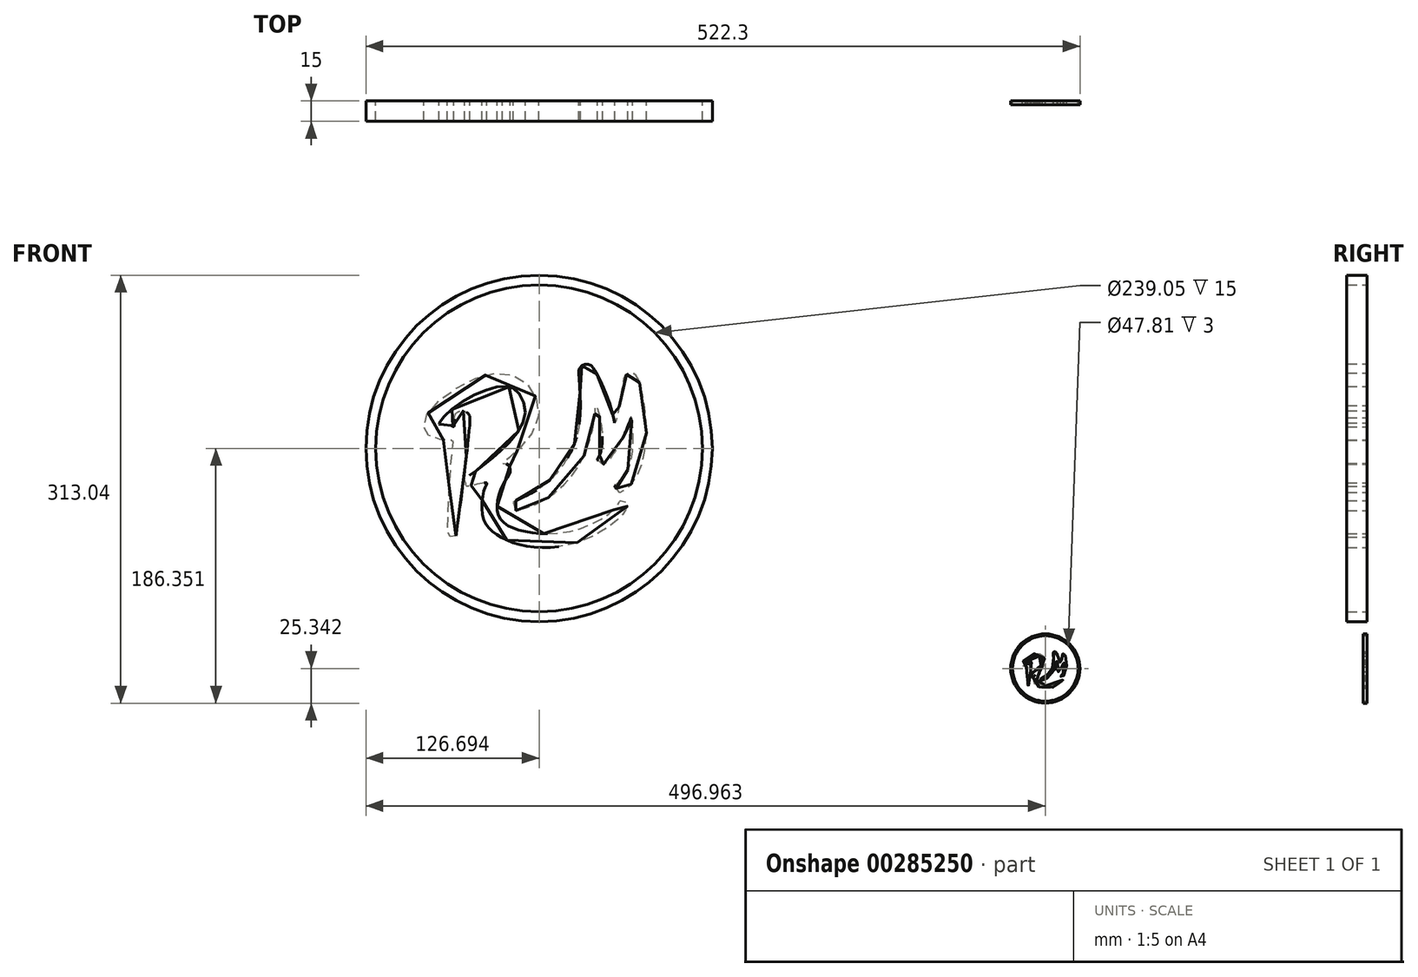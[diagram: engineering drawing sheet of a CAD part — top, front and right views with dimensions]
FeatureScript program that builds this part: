
annotation { "Feature Type Name" : "Feature", "Feature Type Description" : "" }
export const myFeature = defineFeature(function(context is Context, id is Id, definition is map)
    precondition{}
    {
        {
            var Q0;
            Q0=qCreatedBy(makeId("Front.planeOp"),FACE);
            var sketch = newSketch(context, id + "F0", { "sketchPlane" : qUnion([Q0])});
            skLineSegment(sketch, "E0", {"start": v(-226.59, 201.26) * mm, "end": v(-353.59, 201.26) * mm, "construction": true});
            skLineSegment(sketch, "E1", {"start": v(-353.59, 201.26) * mm, "end": v(-353.59, 74.26) * mm, "construction": true});
            skSolve(sketch);
        }
        {
            var Q0;
            Q0=qCreatedBy(makeId("Front.planeOp"),FACE);
            var sketch = newSketch(context, id + "F1", { "sketchPlane" : qUnion([Q0])});
            skCircle(sketch, "E2", {"center": v(-353.59, 201.26) * mm, "radius": 119.53 * mm});
            skCircle(sketch, "E3", {"center": v(-353.59, 201.26) * mm, "radius": 126.69 * mm});
            skFitSpline(sketch, "E4", {"points": [v(-414.44, 137.36) * mm, v(-415.04, 136.58) * mm, v(-419.92, 136.76) * mm, v(-420.66, 137.96) * mm, v(-416.44, 205.5) * mm, v(-416.1, 207.46) * mm, v(-418.73, 207.13) * mm, v(-430.84, 209.18) * mm, v(-437.1, 214.02) * mm, v(-435.75, 225.65) * mm, v(-410.86, 247.16) * mm, v(-380.02, 256.34) * mm, v(-360, 245.85) * mm, v(-354.76, 220.91) * mm, v(-370.6, 198.72) * mm, v(-379.03, 191.38) * mm, v(-380.5, 189.99) * mm, v(-378.95, 190.32) * mm, v(-375.43, 188.51) * mm, v(-374.94, 183.67) * mm, v(-380.51, 173.5) * mm, v(-383.7, 153.36) * mm, v(-368.46, 141.57) * mm, v(-325.38, 141.97) * mm, v(-296.94, 158.74) * mm, v(-294.51, 162.97) * mm, v(-293.79, 163.04) * mm, v(-289.23, 161.97) * mm, v(-288.76, 161.68) * mm, v(-288.83, 160.25) * mm, v(-292.21, 153.27) * mm, v(-323.49, 133.18) * mm, v(-364.56, 130.16) * mm, v(-386.37, 139.44) * mm, v(-394.76, 151.4) * mm, v(-393.66, 170.98) * mm, v(-391.83, 175.15) * mm, v(-391.73, 175.95) * mm, v(-392.42, 176.08) * mm, v(-406.1, 173.54) * mm, v(-406.67, 173.7) * mm, v(-407.93, 177.7) * mm, v(-408.15, 178.84) * mm, v(-407.46, 179.4) * mm, v(-397.98, 186.13) * mm, v(-379.48, 201.61) * mm, v(-363.92, 224.8) * mm, v(-369.63, 243.12) * mm, v(-382.52, 246.44) * mm, v(-411.33, 234.28) * mm, v(-426.28, 220.42) * mm, v(-426.62, 218.9) * mm, v(-425.64, 218.61) * mm, v(-416.76, 217.53) * mm, v(-415.94, 216.96) * mm, v(-415.75, 218.45) * mm, v(-415.38, 224.32) * mm, v(-413.5, 227.54) * mm, v(-408.94, 228.67) * mm, v(-405.01, 226.37) * mm, v(-404.15, 222.66) * mm, v(-409.5, 173.34) * mm, v(-414.44, 137.36) * mm]});
            skFitSpline(sketch, "E5", {"points": [v(-370.72, 163) * mm, v(-372.46, 161.72) * mm, v(-372, 160.21) * mm, v(-371.18, 156.39) * mm, v(-370.95, 155.7) * mm, v(-369.67, 156.04) * mm, v(-355.4, 160.45) * mm, v(-325.94, 186.31) * mm, v(-313.76, 218.8) * mm, v(-312.37, 230.86) * mm, v(-312.14, 232.71) * mm, v(-311.2, 231.09) * mm, v(-307.27, 210.44) * mm, v(-309.97, 195) * mm, v(-310.98, 193.27) * mm, v(-309.94, 192.12) * mm, v(-307.1, 189.75) * mm, v(-306.76, 189.56) * mm, v(-304, 191.25) * mm, v(-293.46, 206.73) * mm, v(-286.73, 222.62) * mm, v(-286.27, 223.66) * mm, v(-285.8, 221.8) * mm, v(-288.16, 187.02) * mm, v(-297.52, 174.6) * mm, v(-298.06, 173.51) * mm, v(-297.87, 172.74) * mm, v(-295.42, 169.51) * mm, v(-295, 169.09) * mm, v(-293.7, 169.38) * mm, v(-282.02, 180.86) * mm, v(-275.71, 226.8) * mm, v(-281.12, 251.88) * mm, v(-282.82, 254.81) * mm, v(-286.62, 256.5) * mm, v(-290.88, 254.27) * mm, v(-292.19, 250.34) * mm, v(-297.4, 221.7) * mm, v(-298.48, 219.8) * mm, v(-298.57, 220.76) * mm, v(-304.83, 242) * mm, v(-313.26, 259.1) * mm, v(-315.79, 262) * mm, v(-320.95, 262.62) * mm, v(-324.19, 259.14) * mm, v(-324.43, 255.22) * mm, v(-323.97, 221.34) * mm, v(-333.48, 193.04) * mm, v(-352.74, 172.4) * mm, v(-370.72, 163) * mm]});
            skSolve(sketch);
        }
        {
            var Q0;
            Q0=makeQuery(id+"F1.imprint","IMPRINT",FACE,{"disambiguationData":[TD([[makeQuery(id+"F1.imprint","IMPRINT",EDGE,{"derivedFrom":sQuery(id+"F1.wireOp",EDGE,"E2")}),-1.0]])]});
            var Q1;
            Q1=makeQuery(id+"F1.imprint","IMPRINT",FACE,{"disambiguationData":[TD([[makeQuery(id+"F1.imprint","IMPRINT",EDGE,{"derivedFrom":sQuery(id+"F1.wireOp",EDGE,"E4")}),-1.0]])]});
            var Q2;
            Q2=makeQuery(id+"F1.imprint","IMPRINT",FACE,{"disambiguationData":[TD([[makeQuery(id+"F1.imprint","IMPRINT",EDGE,{"derivedFrom":sQuery(id+"F1.wireOp",EDGE,"E5")}),1.0]])]});
            extrude(context, id + "F2", {"entities" : qUnion([Q0, Q1, Q2]), "depth" : 15 * mm});
        }
        {
            var Q0;
            Q0=makeQuery(id+"F2.opExtrude","SWEPT_BODY",BODY,{"disambiguationData":[OSD([sQuery(id+"F1.wireOp",EDGE,"E2"),sQuery(id+"F1.wireOp",EDGE,"E3")])]});
            var Q1;
            Q1=makeQuery(id+"F2.opExtrude","SWEPT_BODY",BODY,{"disambiguationData":[OSD([sQuery(id+"F1.wireOp",EDGE,"E4")])]});
            var Q2;
            Q2=makeQuery(id+"F2.opExtrude","SWEPT_BODY",BODY,{"disambiguationData":[OSD([sQuery(id+"F1.wireOp",EDGE,"E5")])]});
            transform(context, id + "F3", {"entities" : qUnion([Q0, Q1, Q2]), "transformType" : TransformType.TRANSLATION_3D, "dx" : 437 * mm, "dy" : 0 * mm, "dz" : 0 * mm, "makeCopy" : true});
        }
        {
            var Q0;
            Q0=makeQuery(id+"F3.opPattern","COPY",BODY,{"derivedFrom":makeQuery(id+"F2.opExtrude","SWEPT_BODY",BODY,{"disambiguationData":[OSD([sQuery(id+"F1.wireOp",EDGE,"E2"),sQuery(id+"F1.wireOp",EDGE,"E3")])]}),"instanceName":"1"});
            var Q1;
            Q1=makeQuery(id+"F3.opPattern","COPY",BODY,{"derivedFrom":makeQuery(id+"F2.opExtrude","SWEPT_BODY",BODY,{"disambiguationData":[OSD([sQuery(id+"F1.wireOp",EDGE,"E4")])]}),"instanceName":"1"});
            var Q2;
            Q2=makeQuery(id+"F3.opPattern","COPY",BODY,{"derivedFrom":makeQuery(id+"F2.opExtrude","SWEPT_BODY",BODY,{"disambiguationData":[OSD([sQuery(id+"F1.wireOp",EDGE,"E5")])]}),"instanceName":"1"});
            var Q3;
            Q3=qCreatedBy(makeId("Origin.pointOp"),VERTEX);
            transform(context, id + "F4", {"entities" : qUnion([Q0, Q1, Q2]), "transformType" : TransformType.SCALE_UNIFORMLY, "scale" : 0.2, "scalePoint" : qUnion([Q3]), "makeCopy" : false});
        }
    });
